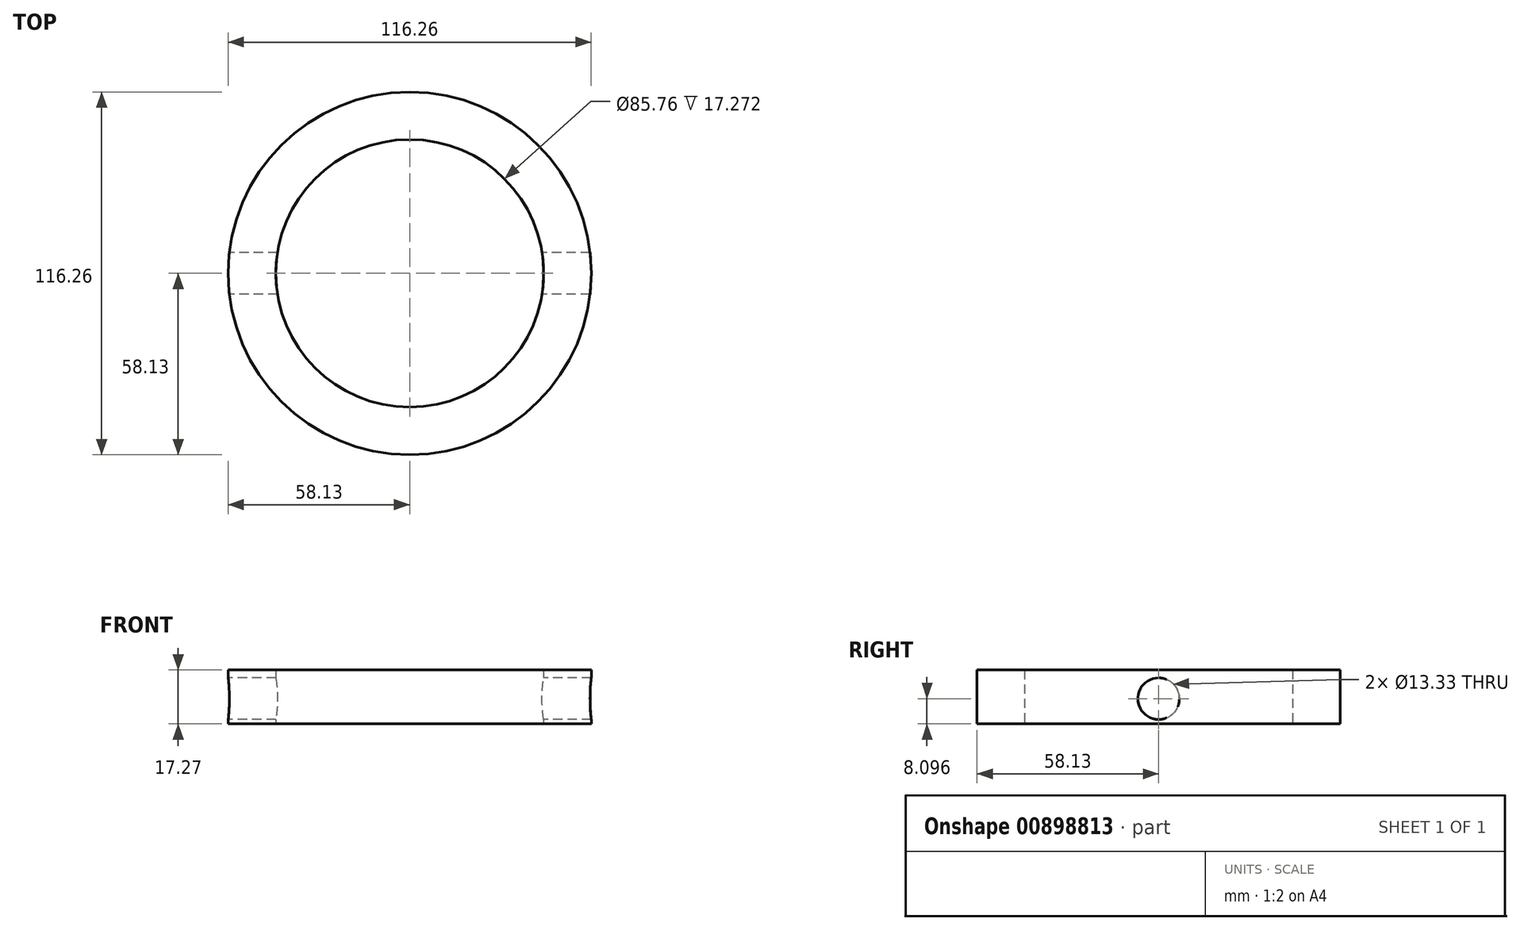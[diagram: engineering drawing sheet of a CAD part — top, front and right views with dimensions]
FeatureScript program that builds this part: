
annotation { "Feature Type Name" : "Feature", "Feature Type Description" : "" }
export const myFeature = defineFeature(function(context is Context, id is Id, definition is map)
    precondition{}
    {
        {
            var Q0;
            Q0=qCreatedBy(makeId("Top.planeOp"),FACE);
            var sketch = newSketch(context, id + "F0", { "sketchPlane" : qUnion([Q0])});
            skCircle(sketch, "E0", {"center": v(0, 0) * mm, "radius": 58.13 * mm});
            skCircle(sketch, "E1", {"center": v(0, 0) * mm, "radius": 42.88 * mm});
            skSolve(sketch);
        }
        {
            var Q0;
            Q0=makeQuery(id+"F0.imprint","IMPRINT",FACE,{"disambiguationData":[TD([[makeQuery(id+"F0.imprint","IMPRINT",EDGE,{"derivedFrom":sQuery(id+"F0.wireOp",EDGE,"E0")}),1.0]])]});
            extrude(context, id + "F1", {"entities" : qUnion([Q0]), "depth" : 17.27 * mm, "offsetDistance" : 25.4 * mm});
        }
        {
            var Q0;
            Q0=qCreatedBy(makeId("Right.planeOp"),FACE);
            var sketch = newSketch(context, id + "F2", { "sketchPlane" : qUnion([Q0])});
            skCircle(sketch, "E2", {"center": v(0, 8.34) * mm, "radius": 6.03 * mm});
            skSolve(sketch);
        }
        {
            var Q0;
            Q0 = qSketchRegion(id + "F2", true);
            extrude(context, id + "F3", {"entities" : qUnion([Q0]), "operationType" : NewBodyOperationType.REMOVE, "depth" : 121.92 * mm, "offsetDistance" : 25.4 * mm});
        }
        {
            var Q0;
            Q0=qCreatedBy(makeId("Right.planeOp"),FACE);
            var sketch = newSketch(context, id + "F4", { "sketchPlane" : qUnion([Q0])});
            skCircle(sketch, "E3", {"center": v(0, 8.1) * mm, "radius": 6.67 * mm});
            skSolve(sketch);
        }
        {
            var Q0;
            Q0 = qSketchRegion(id + "F4", true);
            extrude(context, id + "F5", {"entities" : qUnion([Q0]), "operationType" : NewBodyOperationType.REMOVE, "endBound" : BoundingType.SYMMETRIC, "depth" : 163.58 * mm, "offsetDistance" : 25.4 * mm});
        }
    });
